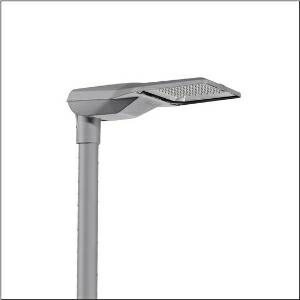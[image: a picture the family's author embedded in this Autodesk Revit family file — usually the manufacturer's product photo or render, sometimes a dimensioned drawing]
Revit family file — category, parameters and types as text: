
# Revit family: streetlight_sl_21_iq_midi___st1_5a_5xe3p31g08mb_98ff
name_source: partatom
category: Lighting Fixtures
units: mm (PartAtom-declared; Revit-internal decimal feet)

## family parameters
Cut with Voids When Loaded = No
Host = Face
Light Source = No
Part Type = Normal
Room Calculation Point = No
Round Connector Dimension = Use Diameter
Shared = No

## types (1)
- --- (1 x LED, 19170 lm, 146.7 W, 3000K)
    Apparent Load = 147 VA
    CIE Flux Codes = 22 53 95 100 100
    Color Rendering = 70
    Color Temperature = 3000K
    Default Elevation = 1800 mm
    Description = Streetlight SL 21 iQ midi, mast luminaire, primary light control with lens, of PMMA, primary optical cover: cover, of toughened safety glass, transparent, light distribution: ST1.5a, light emission: direct distribution, primary light characteristic: asymmetric, installation type: post-top, side-entry, LED, High Power LED, rated luminous flux: 19.170lm, luminous efficacy: 131lm/W, light colour: 730, colour temperature: 3000K, control gear: iQ Street-Remote, control: Street-Remote, Auto-Match, Temp-Guard, Lumen-Switch, Night-Set, Smart-Wire, Light-Fading, Desk-Remote (wireless, voltage-free reading and setting of iQ features in the workshop via application-optimized NFC function/RFID function), optimised constant luminous flux control (CLO 2.0), pre-setting: linear dimming characteristic, mains connection: 230..240V, AC, 50/60Hz, start of lifetime: 147W, end of service life: 161W, reduction: 62W, luminaire housing, of diecast aluminium, powder-coated, SITECO metallic grey (DB 702S), corrosivity category C5 high according to DIN EN ISO 12944, please order mast flange separately, inclination adjustable: 0°, 5°, 10°, 15°, sealing non-destructively replaceable, multi-level sealing system, length: 644mm, width: 335mm, height: 110mm, mast flange for spigot size: 42mm (side-entry): 5XC10008XM4, 60/48mm (side-entry/post-top): 5XC10108XM2, 76/60mm (side-entry/post-top): 5XC10108XM1, mounting height: 4..8m, protection rating (complete): IP66, insulation class (complete): insulation class II (safety insulation), certification: CE, ENEC, ENEC+, VDE, impact resistance: IK10, permissible operating ambient temperature for outdoor applications: -40..+50°C, standard-compliant lighting for roads and squares, packaging unit: 1 piece

Light Distribution: ST1.5a
    Height = 111 mm
    Lamp = 1 x LED
    Lamp Light Flux = 19170 lm
    Lamp Power = 146.7 W
    Lamp count = 1
    Length = 644 mm
    Luminous efficacy = 131 lm/W
    Manufacturer = Siteco
    ModVariant = No
    Model = 5XE3P31G08MB
    Number of Poles = 1
    OnlyDefault = Yes
    Power Factor = 1
    Product Name = Streetlight SL 21 iQ midi | ST1.5a
    Product group = mast luminaire | pylon top
    ProductGroupID = 6100
    Protection Class = Protection class II
    Protection Degree = IP 66
    RLX_Detail_Level = 1
    RLX_Emergency_Light_Flux = 0 lm
    RLX_Emergency_Type = 0
    RLX_Emergency_Type_DB = No
    RlxData = <blob elided: 30429 chars, md5=7f346043>
    Socket = socket
    Standby Power = 0 W
    System Light Flux = 19169 lm
    System Power = 147 W
    Type Comments = factory setting: luminous flux: 100 % | dim-lin: 254 | 753 mA
    Type Image = l_1004298.jpg
    URL = http://relux.com
    VarID = @adj_175773
    Voltage = 0 V
    Weight = 0.00 kg
    Width = 336 mm

## geometry (parser evidence)
native form markers: Blend x4, Sweep x10
no freeform markers — native parametric forms only
